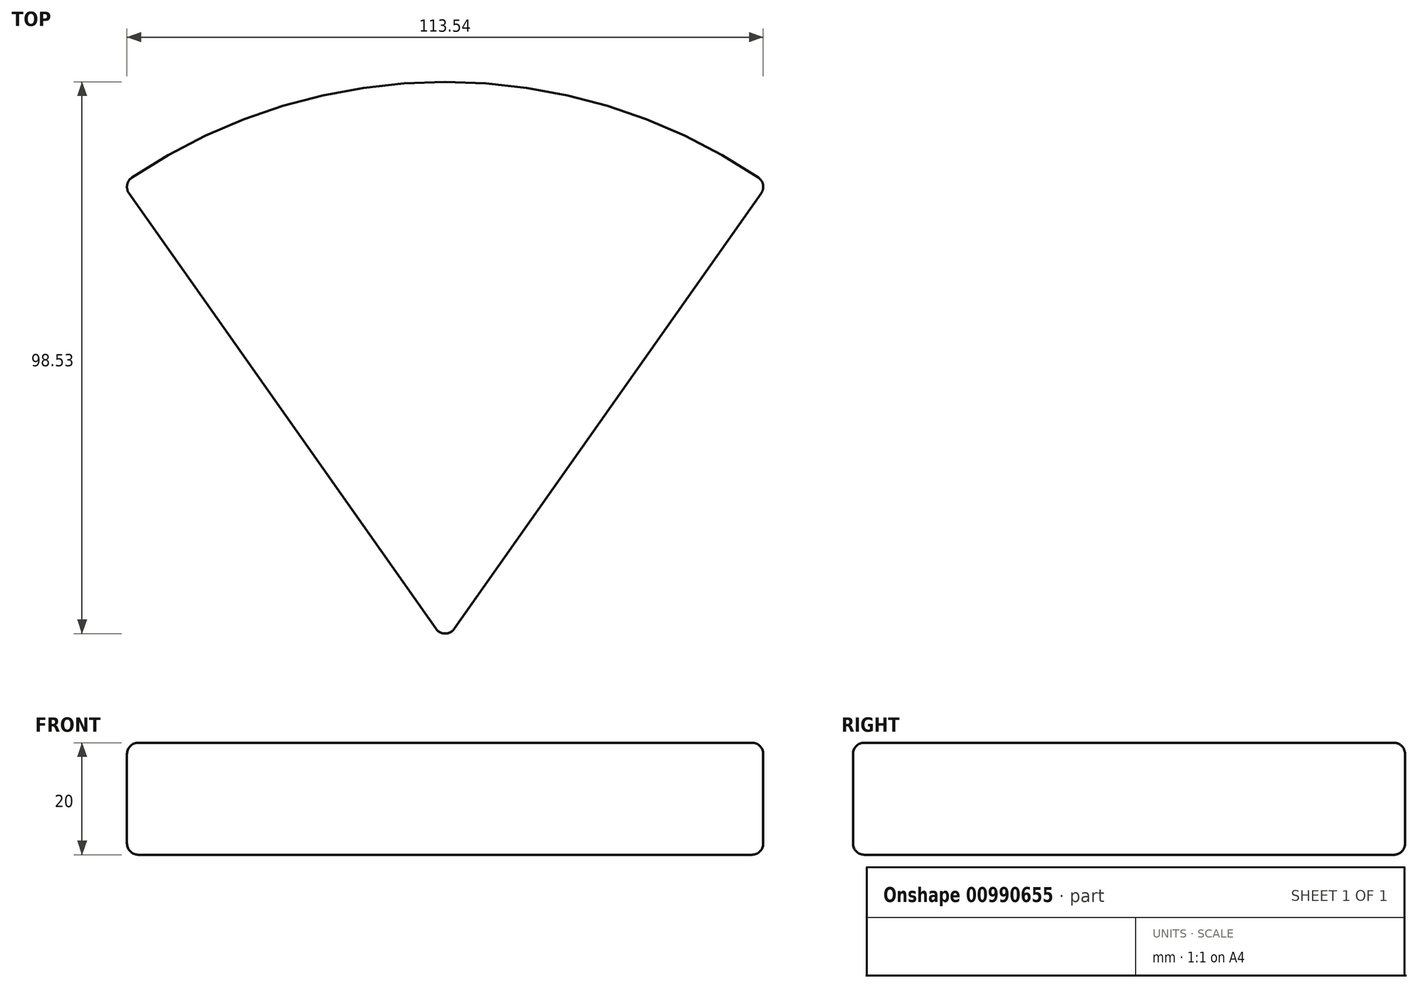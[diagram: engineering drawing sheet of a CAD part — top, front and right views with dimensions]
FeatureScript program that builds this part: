
annotation { "Feature Type Name" : "Feature", "Feature Type Description" : "" }
export const myFeature = defineFeature(function(context is Context, id is Id, definition is map)
    precondition{}
    {
        {
            var Q0;
            Q0=qCreatedBy(makeId("Top.planeOp"),FACE);
            var sketch = newSketch(context, id + "F0", { "sketchPlane" : qUnion([Q0])});
            skLineSegment(sketch, "E0", {"start": v(0, -53.36) * mm, "end": v(-57.57, 28.4) * mm});
            skLineSegment(sketch, "E1.MirrorCS", {"start": v(0, -53.36) * mm, "end": v(57.57, 28.4) * mm});
            skArc(sketch, "E2", {"start": v(-57.57, 28.4) * mm, "mid": v(0, 46.64) * mm, "end": v(57.57, 28.4) * mm});
            skSolve(sketch);
        }
        {
            var Q0;
            Q0=makeQuery(id+"F0.imprint","IMPRINT",FACE,{"disambiguationData":[TD([[makeQuery(id+"F0.imprint","IMPRINT",EDGE,{"derivedFrom":sQuery(id+"F0.wireOp",EDGE,"E0")}),-1.0]])]});
            extrude(context, id + "F1", {"entities" : qUnion([Q0]), "endBound" : BoundingType.SYMMETRIC, "depth" : 20 * mm, "offsetDistance" : 25.4 * mm});
        }
        {
            var Q0;
            Q0=makeQuery(id+"F1.opExtrude","CAP_EDGE",EDGE,{"disambiguationData":[OSD([sQuery(id+"F0.wireOp",EDGE,"E0")])],"isStart":false});
            var Q1;
            Q1=makeQuery(id+"F1.opExtrude","CAP_EDGE",EDGE,{"disambiguationData":[OSD([sQuery(id+"F0.wireOp",EDGE,"E2")])],"isStart":false});
            var Q2;
            Q2=makeQuery(id+"F1.opExtrude","CAP_EDGE",EDGE,{"disambiguationData":[OSD([sQuery(id+"F0.wireOp",EDGE,"E1.MirrorCS")])],"isStart":false});
            var Q3;
            Q3=makeQuery(id+"F1.opExtrude","SWEPT_EDGE",EDGE,{"disambiguationData":[OSD([sQuery(id+"F0.wireOp",EDGE,"E0"),sQuery(id+"F0.wireOp",EDGE,"E1.MirrorCS")])]});
            var Q4;
            Q4=makeQuery(id+"F1.opExtrude","CAP_EDGE",EDGE,{"disambiguationData":[OSD([sQuery(id+"F0.wireOp",EDGE,"E1.MirrorCS")])],"isStart":true});
            var Q5;
            Q5=makeQuery(id+"F1.opExtrude","CAP_EDGE",EDGE,{"disambiguationData":[OSD([sQuery(id+"F0.wireOp",EDGE,"E0")])],"isStart":true});
            var Q6;
            Q6=makeQuery(id+"F1.opExtrude","SWEPT_EDGE",EDGE,{"disambiguationData":[OSD([sQuery(id+"F0.wireOp",EDGE,"E0"),sQuery(id+"F0.wireOp",EDGE,"E2")])]});
            var Q7;
            Q7=makeQuery(id+"F1.opExtrude","CAP_EDGE",EDGE,{"disambiguationData":[OSD([sQuery(id+"F0.wireOp",EDGE,"E2")])],"isStart":true});
            var Q8;
            Q8=makeQuery(id+"F1.opExtrude","SWEPT_EDGE",EDGE,{"disambiguationData":[OSD([sQuery(id+"F0.wireOp",EDGE,"E1.MirrorCS"),sQuery(id+"F0.wireOp",EDGE,"E2")])]});
            fillet(context, id + "F2", {"entities" : qUnion([Q0, Q1, Q2, Q3, Q4, Q5, Q6, Q7, Q8]), "radius" : 2 * mm, "tangentPropagation" : true, "allowEdgeOverflow" : false});
        }
    });
